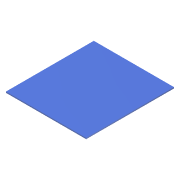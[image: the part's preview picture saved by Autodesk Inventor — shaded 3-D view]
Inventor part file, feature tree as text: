
AUTODESK INVENTOR PART (.ipt)
format: ipt  version: 2014 (Build 180170000, 170)  size: 68,096 bytes
history: native  units: mm
features: extrude x1, sketch x1
ambient origin geometry x8: Origin, YZ Plane, XZ Plane, XY Plane, X Axis, Y Axis, Z Axis, Center Point
bodies: Solid1 (feature_tree)
feature tree (2):
  extrude  "Extrusion1"  Depth=210.0mm
  sketch  "Sketch1"  dims[d0=230.0mm d1=210.0mm d2=3.0mm d3=0.0mm]
